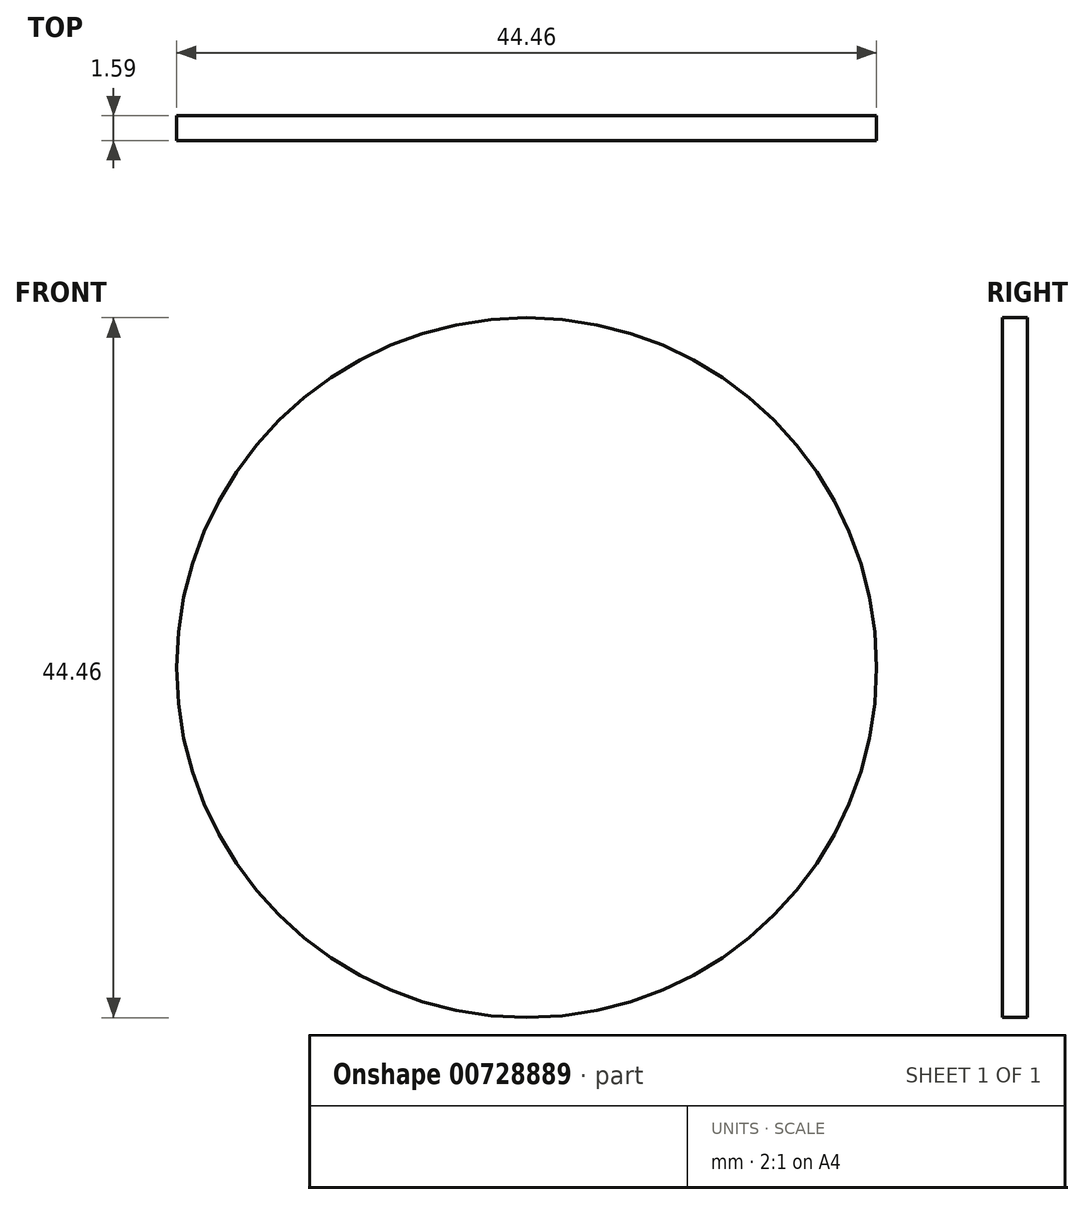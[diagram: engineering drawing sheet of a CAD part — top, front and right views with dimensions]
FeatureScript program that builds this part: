
annotation { "Feature Type Name" : "Feature", "Feature Type Description" : "" }
export const myFeature = defineFeature(function(context is Context, id is Id, definition is map)
    precondition{}
    {
        {
            var Q0;
            Q0=qCreatedBy(makeId("Front.planeOp"),FACE);
            var sketch = newSketch(context, id + "F0", { "sketchPlane" : qUnion([Q0])});
            skCircle(sketch, "E0", {"center": v(0, 0) * mm, "radius": 22.23 * mm});
            skSolve(sketch);
        }
        {
            var Q0;
            Q0 = qSketchRegion(id + "F0", true);
            extrude(context, id + "F1", {"entities" : qUnion([Q0]), "depth" : 1.59 * mm, "offsetDistance" : 25.4 * mm});
        }
    });
